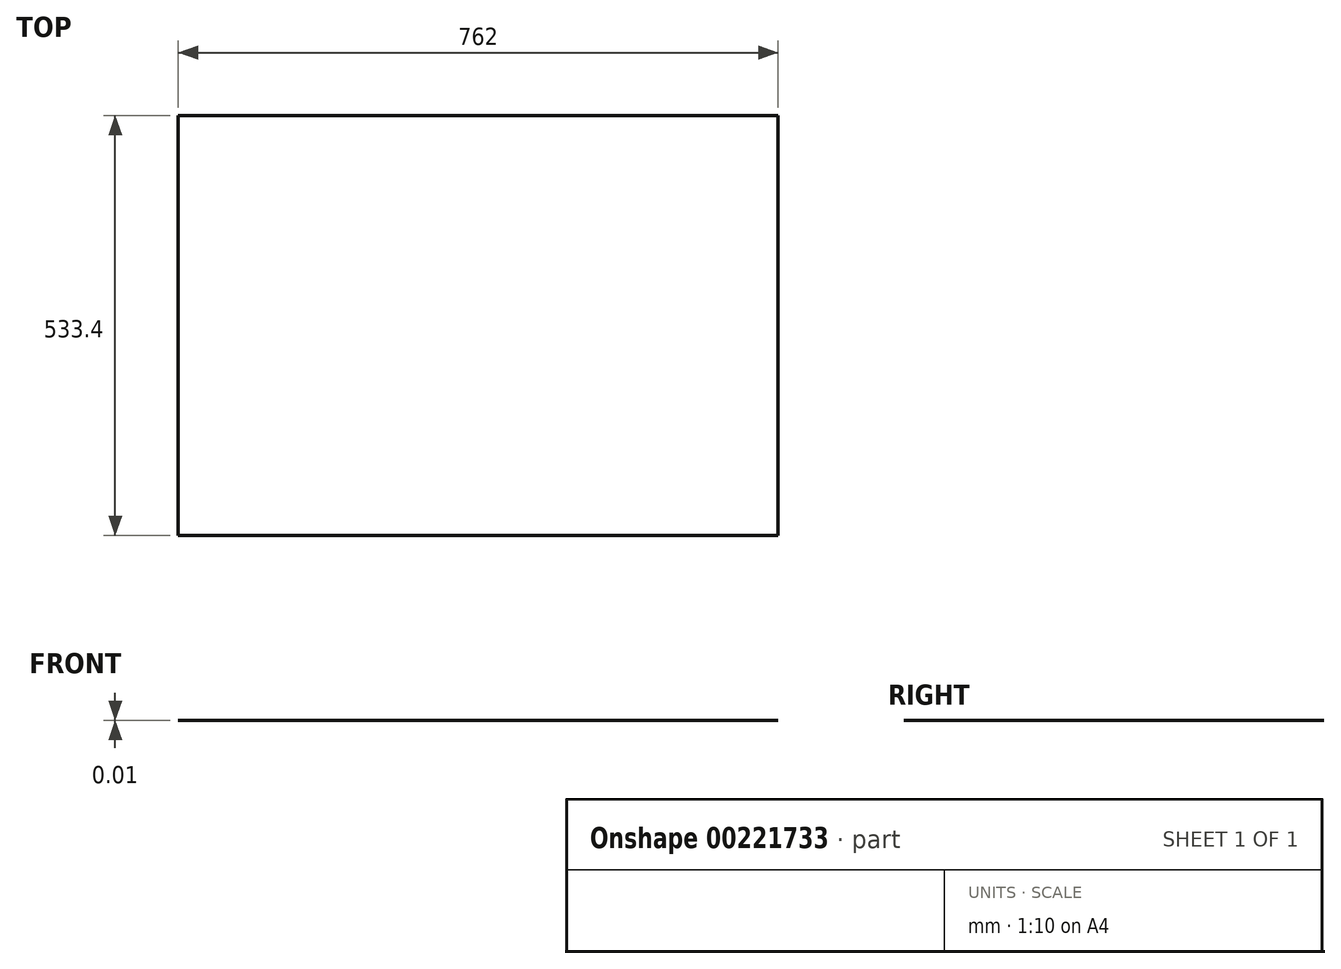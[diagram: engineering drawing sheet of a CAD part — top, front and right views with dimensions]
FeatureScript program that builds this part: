
annotation { "Feature Type Name" : "Feature", "Feature Type Description" : "" }
export const myFeature = defineFeature(function(context is Context, id is Id, definition is map)
    precondition{}
    {
        {
            var Q0;
            Q0=qCreatedBy(makeId("Top.planeOp"),FACE);
            var sketch = newSketch(context, id + "F0", { "sketchPlane" : qUnion([Q0])});
            skLineSegment(sketch, "E0.bottom", {"start": v(-149.56, -41.45) * mm, "end": v(612.44, -41.45) * mm});
            skLineSegment(sketch, "E0.top", {"start": v(-149.56, 491.95) * mm, "end": v(612.44, 491.95) * mm});
            skLineSegment(sketch, "E0.left", {"start": v(-149.56, -41.45) * mm, "end": v(-149.56, 491.95) * mm});
            skLineSegment(sketch, "E0.right", {"start": v(612.44, -41.45) * mm, "end": v(612.44, 491.95) * mm});
            skSolve(sketch);
        }
        {
            var Q0;
            Q0 = qSketchRegion(id + "F0", true);
            extrude(context, id + "F1", {"entities" : qUnion([Q0]), "oppositeDirection" : true, "depth" : 3 / 406.4 * mm});
        }
    });
